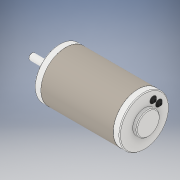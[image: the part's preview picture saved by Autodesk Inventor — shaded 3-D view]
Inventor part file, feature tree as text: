
AUTODESK INVENTOR PART (.ipt)
format: ipt  version: 2017 (Build 210142000, 142)  size: 165,888 bytes
history: native  units: in
note: dims shown in document units (in); Inventor stores cm internally (conversion verified against a paired STEP export)
features: chamfer x1
ambient origin geometry x8: Origin, YZ Plane, XZ Plane, XY Plane, X Axis, Y Axis, Z Axis, Center Point
bodies: Solid1 (feature_tree)
feature tree (1):
  chamfer  "Chamfer3"  [1 undecoded]
note: 1 required parameter value undecoded (feature->parameter linkage not recoverable at this tier; creation-order binding heuristic only, values carry confidence <= 0.55)
